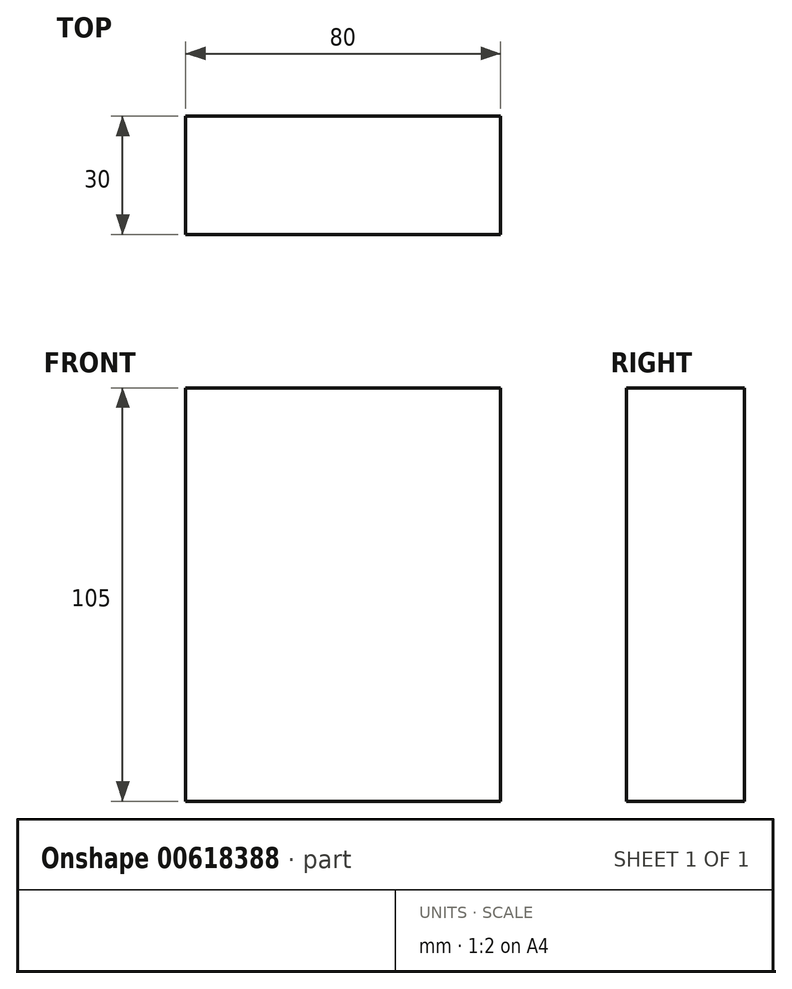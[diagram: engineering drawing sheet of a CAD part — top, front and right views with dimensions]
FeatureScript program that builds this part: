
annotation { "Feature Type Name" : "Feature", "Feature Type Description" : "" }
export const myFeature = defineFeature(function(context is Context, id is Id, definition is map)
    precondition{}
    {
        {
            var Q0;
            Q0=qCreatedBy(makeId("Top.planeOp"),FACE);
            var sketch = newSketch(context, id + "F0", { "sketchPlane" : qUnion([Q0])});
            skLineSegment(sketch, "E0.bottom", {"start": v(0, 0) * mm, "end": v(80, 0) * mm});
            skLineSegment(sketch, "E0.top", {"start": v(0, 30) * mm, "end": v(80, 30) * mm});
            skLineSegment(sketch, "E0.left", {"start": v(0, 0) * mm, "end": v(0, 30) * mm});
            skLineSegment(sketch, "E0.right", {"start": v(80, 0) * mm, "end": v(80, 30) * mm});
            skSolve(sketch);
        }
        {
            var Q0;
            Q0=makeQuery(id+"F0.imprint","IMPRINT",FACE,{"disambiguationData":[TD([[makeQuery(id+"F0.imprint","IMPRINT",EDGE,{"derivedFrom":sQuery(id+"F0.wireOp",EDGE,"E0.bottom")}),1.0]])]});
            extrude(context, id + "F1", {"entities" : qUnion([Q0]), "depth" : 105 * mm, "offsetDistance" : 25 * mm});
        }
    });
